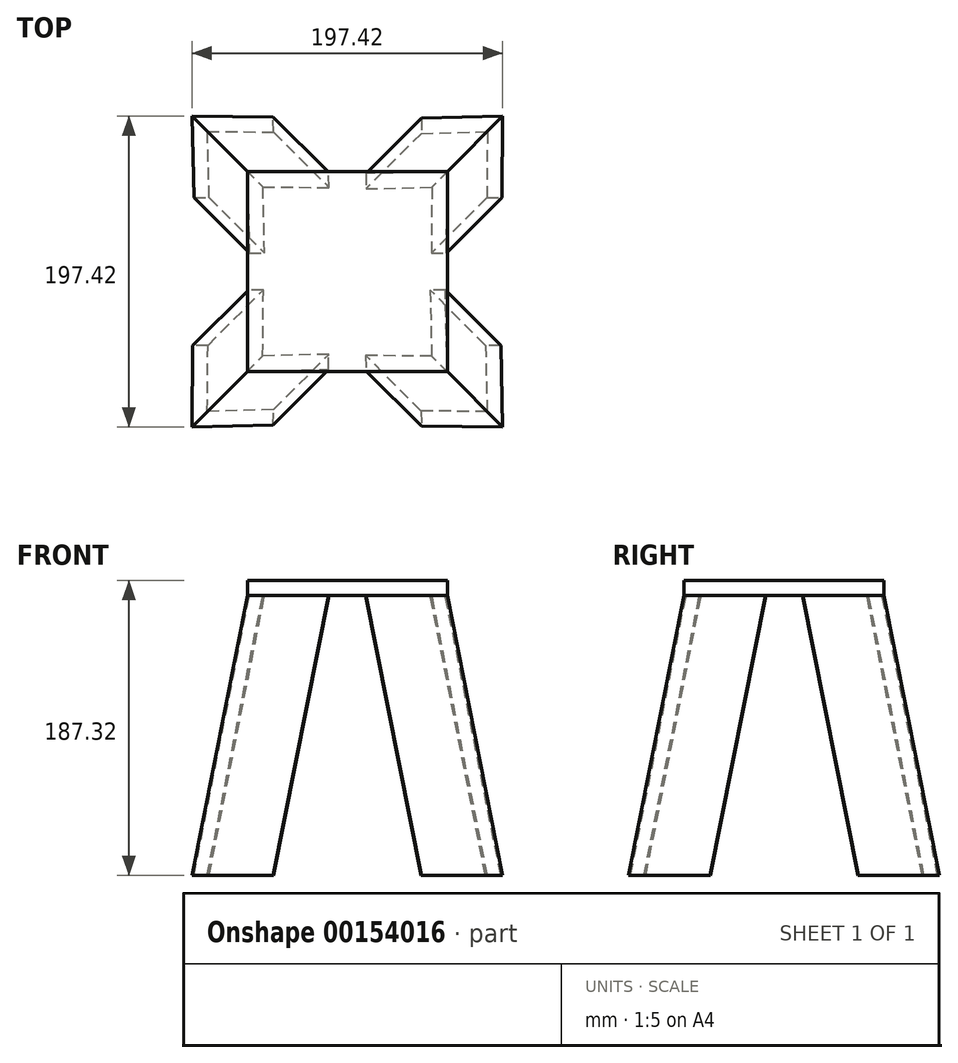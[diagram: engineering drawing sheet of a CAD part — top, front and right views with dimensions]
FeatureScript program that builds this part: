
annotation { "Feature Type Name" : "Feature", "Feature Type Description" : "" }
export const myFeature = defineFeature(function(context is Context, id is Id, definition is map)
    precondition{}
    {
        {
            var Q0;
            Q0=qCreatedBy(makeId("Top.planeOp"),FACE);
            var sketch = newSketch(context, id + "F0", { "sketchPlane" : qUnion([Q0])});
            skLineSegment(sketch, "E0.bottom", {"start": v(63.5, -63.5) * mm, "end": v(-63.5, -63.5) * mm});
            skLineSegment(sketch, "E0.top", {"start": v(63.5, 63.5) * mm, "end": v(-63.5, 63.5) * mm});
            skLineSegment(sketch, "E0.left", {"start": v(63.5, -63.5) * mm, "end": v(63.5, 63.5) * mm});
            skLineSegment(sketch, "E0.right", {"start": v(-63.5, -63.5) * mm, "end": v(-63.5, 63.5) * mm});
            skPoint(sketch, "E0.middle", {"position": v(0, 0) * mm});
            skSolve(sketch);
        }
        {
            var Q0;
            Q0 = qSketchRegion(id + "F0", true);
            extrude(context, id + "F1", {"entities" : qUnion([Q0]), "endBound" : BoundingType.SYMMETRIC, "depth" : 3 / 203.2 * mm, "offsetDistance" : 25.4 * mm});
        }
        {
            var Q0;
            Q0=makeQuery(id+"F1.opExtrude","SWEPT_EDGE",EDGE,{"disambiguationData":[OSD([sQuery(id+"F0.wireOp",EDGE,"E0.bottom"),sQuery(id+"F0.wireOp",EDGE,"E0.left")])]});
            var Q1;
            Q1=makeQuery(id+"F1.opExtrude","SWEPT_EDGE",EDGE,{"disambiguationData":[OSD([sQuery(id+"F0.wireOp",EDGE,"E0.top"),sQuery(id+"F0.wireOp",EDGE,"E0.right")])]});
            cPlane(context, id + "F2", {"entities" : qUnion([Q0, Q1]), "cplaneType" : CPlaneType.LINE_ANGLE, "offset" : 25.4 * mm, "angle" : 0 * degree, "width" : 152.4 * mm, "height" : 152.4 * mm});
        }
        {
            var Q0;
            Q0=qCreatedBy(makeId("Top.planeOp"),FACE);
            var sketch = newSketch(context, id + "F3", { "sketchPlane" : qUnion([Q0])});
            skLineSegment(sketch, "E1", {"start": v(36.83, 0) * mm, "end": v(0, 0) * mm, "construction": true});
            skLineSegment(sketch, "E2", {"start": v(0, 0) * mm, "end": v(35.44, 35.44) * mm});
            skSolve(sketch);
        }
        {
            var Q0;
            Q0=sQuery(id+"F3.wireOp",EDGE,"E2");
            var Q1;
            Q1=qCreatedBy(makeId("Top.planeOp"),FACE);
            cPlane(context, id + "F4", {"entities" : qUnion([Q0, Q1]), "cplaneType" : CPlaneType.LINE_ANGLE, "offset" : 25.4 * mm, "angle" : 10 * degree, "oppositeDirection" : true, "width" : 152.4 * mm, "height" : 152.4 * mm});
        }
        {
            var Q0;
            Q0=qCreatedBy(id+"F4.planeOp",FACE);
            cPlane(context, id + "F5", {"entities" : qUnion([Q0]), "cplaneType" : CPlaneType.OFFSET, "offset" : 215.9 * mm, "width" : 152.4 * mm, "height" : 152.4 * mm});
        }
        {
            var Q0;
            Q0=qCreatedBy(id+"F5.planeOp",FACE);
            var sketch = newSketch(context, id + "F6", { "sketchPlane" : qUnion([Q0])});
            skLineSegment(sketch, "E3", {"start": v(24.24, 76.2) * mm, "end": v(75.04, 76.2) * mm});
            skLineSegment(sketch, "E4", {"start": v(75.04, 76.2) * mm, "end": v(75.04, 25.4) * mm});
            skLineSegment(sketch, "E5", {"start": v(75.04, 25.4) * mm, "end": v(65.52, 25.4) * mm});
            skLineSegment(sketch, "E6", {"start": v(65.52, 25.4) * mm, "end": v(65.52, 66.67) * mm});
            skLineSegment(sketch, "E7", {"start": v(65.52, 66.67) * mm, "end": v(24.24, 66.67) * mm});
            skLineSegment(sketch, "E8", {"start": v(24.24, 66.67) * mm, "end": v(24.24, 76.2) * mm});
            skLineSegment(sketch, "E9", {"start": v(0, 0) * mm, "end": v(0, 96.6) * mm, "construction": true});
            skLineSegment(sketch, "E10", {"start": v(0, 0) * mm, "end": v(100.3, 0) * mm, "construction": true});
            skLineSegment(sketch, "E11", {"start": v(80.7, 81.94) * mm, "end": v(-46.07, -46.78) * mm, "construction": true});
            skSolve(sketch);
        }
        {
            var Q0;
            Q0=qCreatedBy(id+"F2.planeOp",FACE);
            var sketch = newSketch(context, id + "F7", { "sketchPlane" : qUnion([Q0])});
            skLineSegment(sketch, "E12", {"start": v(-80.77, 27.48) * mm, "end": v(-142.81, -194.05) * mm});
            skSolve(sketch);
        }
        {
            var Q0;
            Q0 = qSketchRegion(id + "F6", true);
            var Q1;
            Q1 = qConstructionFilter(qBodyType(qCreatedBy(id + "F7" ,EDGE), BodyType.WIRE), ConstructionObject.NO);
            sweep(context, id + "F8", {"operationType" : NewBodyOperationType.ADD, "profiles" : qUnion([Q0]), "path" : qUnion([Q1])});
        }
        {
            var Q0;
            Q0=qCreatedBy(makeId("Front.planeOp"),FACE);
            var sketch = newSketch(context, id + "F9", { "sketchPlane" : qUnion([Q0])});
            skLineSegment(sketch, "E13", {"start": v(0, 0) * mm, "end": v(0, -99.1) * mm});
            skSolve(sketch);
        }
        {
            var Q0;
            Q0=makeQuery(id+"F1.opExtrude","SWEPT_BODY",BODY,{"disambiguationData":[OSD([sQuery(id+"F0.wireOp",EDGE,"E0.bottom"),sQuery(id+"F0.wireOp",EDGE,"E0.top"),sQuery(id+"F0.wireOp",EDGE,"E0.left"),sQuery(id+"F0.wireOp",EDGE,"E0.right")])]});
            var Q1;
            Q1=sQuery(id+"F9.wireOp",EDGE,"E13");
            circularPattern(context, id + "F10", {"entities" : qUnion([Q0]), "axis" : qUnion([Q1]), "angle" : 360 * degree, "instanceCount" : 4, "equalSpace" : true});
        }
        {
            var Q0;
            Q0=qCreatedBy(makeId("Front.planeOp"),FACE);
            var sketch = newSketch(context, id + "F11", { "sketchPlane" : qUnion([Q0])});
            skLineSegment(sketch, "E14.bottom", {"start": v(-125.38, -182.56) * mm, "end": v(131.24, -182.56) * mm});
            skLineSegment(sketch, "E14.top", {"start": v(-125.38, -229.93) * mm, "end": v(131.24, -229.93) * mm});
            skLineSegment(sketch, "E14.left", {"start": v(-125.38, -182.56) * mm, "end": v(-125.38, -229.93) * mm});
            skLineSegment(sketch, "E14.right", {"start": v(131.24, -182.56) * mm, "end": v(131.24, -229.93) * mm});
            skLineSegment(sketch, "E15.bottom", {"start": v(-110.74, 46.05) * mm, "end": v(97.66, 46.05) * mm});
            skLineSegment(sketch, "E15.top", {"start": v(-110.74, -4.76) * mm, "end": v(97.66, -4.76) * mm});
            skLineSegment(sketch, "E15.left", {"start": v(-110.74, 46.05) * mm, "end": v(-110.74, -4.76) * mm});
            skLineSegment(sketch, "E15.right", {"start": v(97.66, 46.05) * mm, "end": v(97.66, -4.76) * mm});
            skSolve(sketch);
        }
        {
            var Q0;
            Q0 = qSketchRegion(id + "F11", true);
            extrude(context, id + "F12", {"entities" : qUnion([Q0]), "operationType" : NewBodyOperationType.REMOVE, "endBound" : BoundingType.THROUGH_ALL, "oppositeDirection" : true, "depth" : 25.4 * mm, "offsetDistance" : 25.4 * mm, "hasSecondDirection" : true, "secondDirectionBound" : SecondDirectionBoundingType.THROUGH_ALL, "secondDirectionOppositeDirection" : false, "secondDirectionDepth" : 25.4 * mm});
        }
        {
            var Q0;
            {var subQ0=sQuery(id+"F7.wireOp",EDGE,"E12");Q0=makeQuery(id+"F12.boolean.opBoolean","COPY",FACE,{"disambiguationData":[TD([makeQuery(id+"F8.opSweep","SWEPT_FACE",FACE,{"disambiguationData":[OSD([sQuery(id+"F6.wireOp",EDGE,"E3"),subQ0])]})])],"derivedFrom":makeQuery(id+"F12.opExtrude","SWEPT_FACE",FACE,{"disambiguationData":[OSD([sQuery(id+"F11.wireOp",EDGE,"E15.top")])]})});}
            var sketch = newSketch(context, id + "F13", { "sketchPlane" : qUnion([Q0])});
            skLineSegment(sketch, "E16.bottom", {"start": v(63.5, -63.5) * mm, "end": v(-63.5, -63.5) * mm});
            skLineSegment(sketch, "E16.top", {"start": v(63.5, 63.5) * mm, "end": v(-63.5, 63.5) * mm});
            skLineSegment(sketch, "E16.left", {"start": v(63.5, -63.5) * mm, "end": v(63.5, 63.5) * mm});
            skLineSegment(sketch, "E16.right", {"start": v(-63.5, -63.5) * mm, "end": v(-63.5, 63.5) * mm});
            skPoint(sketch, "E16.middle", {"position": v(0, 0) * mm});
            skSolve(sketch);
        }
        {
            var Q0;
            Q0 = qSketchRegion(id + "F13", true);
            extrude(context, id + "F14", {"entities" : qUnion([Q0]), "operationType" : NewBodyOperationType.ADD, "depth" : 9.52 * mm, "offsetDistance" : 25.4 * mm});
        }
    });
